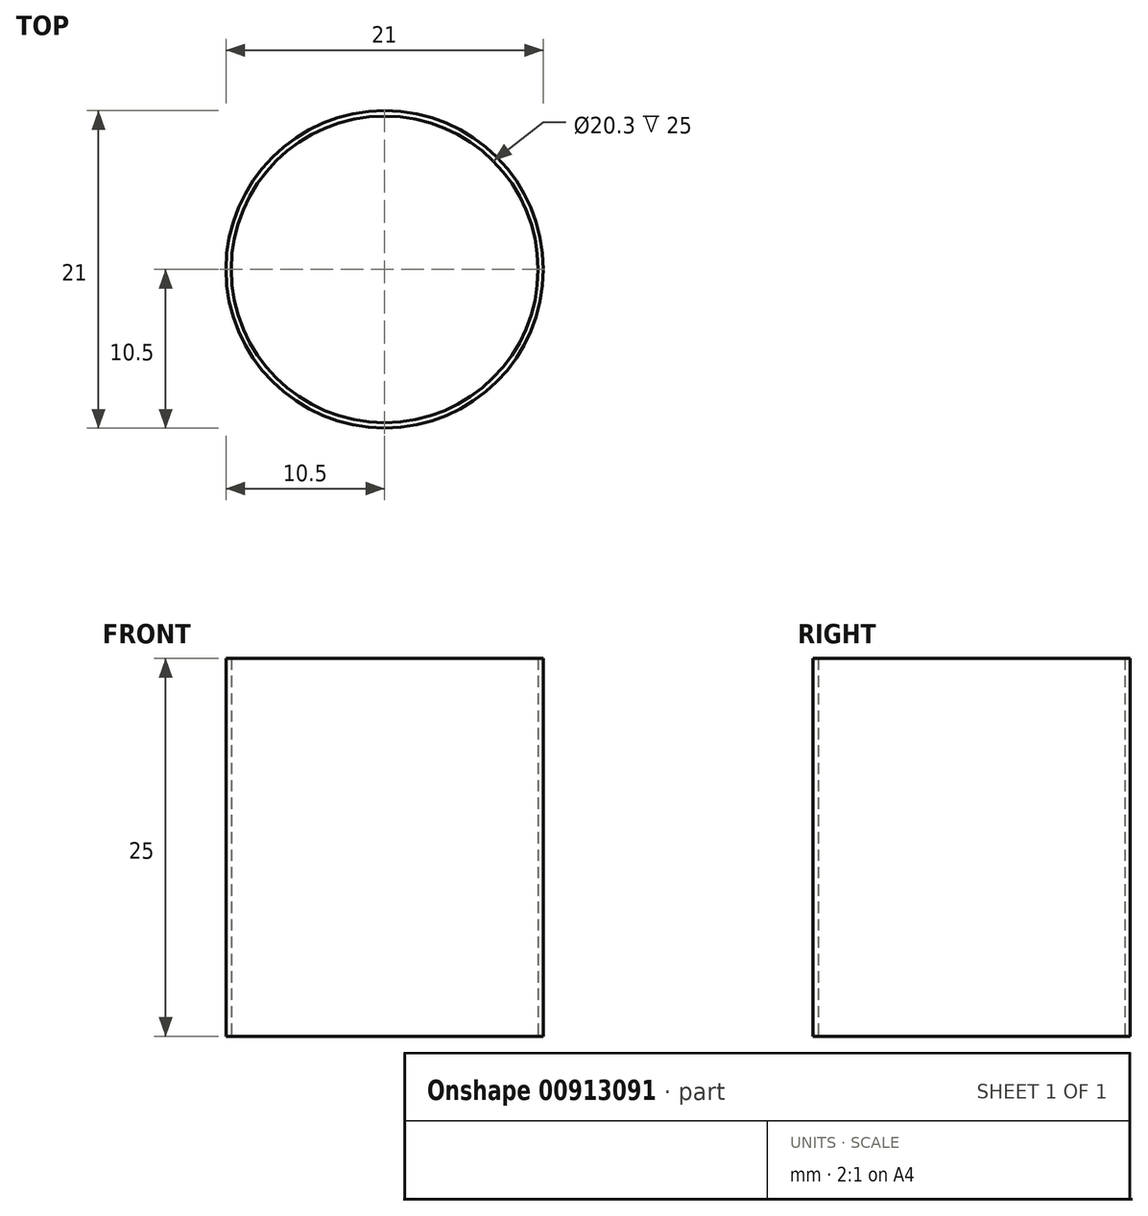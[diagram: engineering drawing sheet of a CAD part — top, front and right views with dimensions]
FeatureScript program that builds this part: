
annotation { "Feature Type Name" : "Feature", "Feature Type Description" : "" }
export const myFeature = defineFeature(function(context is Context, id is Id, definition is map)
    precondition{}
    {
        {
            var Q0;
            Q0=qCreatedBy(makeId("Top.planeOp"),FACE);
            var sketch = newSketch(context, id + "F0", { "sketchPlane" : qUnion([Q0])});
            skCircle(sketch, "E0", {"center": v(0, 0) * mm, "radius": 10.15 * mm});
            skCircle(sketch, "E1", {"center": v(0, 0) * mm, "radius": 10.5 * mm});
            skSolve(sketch);
        }
        {
            var Q0;
            Q0 = qSketchRegion(id + "F0", true);
            extrude(context, id + "F1", {"entities" : qUnion([Q0]), "depth" : 25 * mm, "offsetDistance" : 25 * mm});
        }
    });
